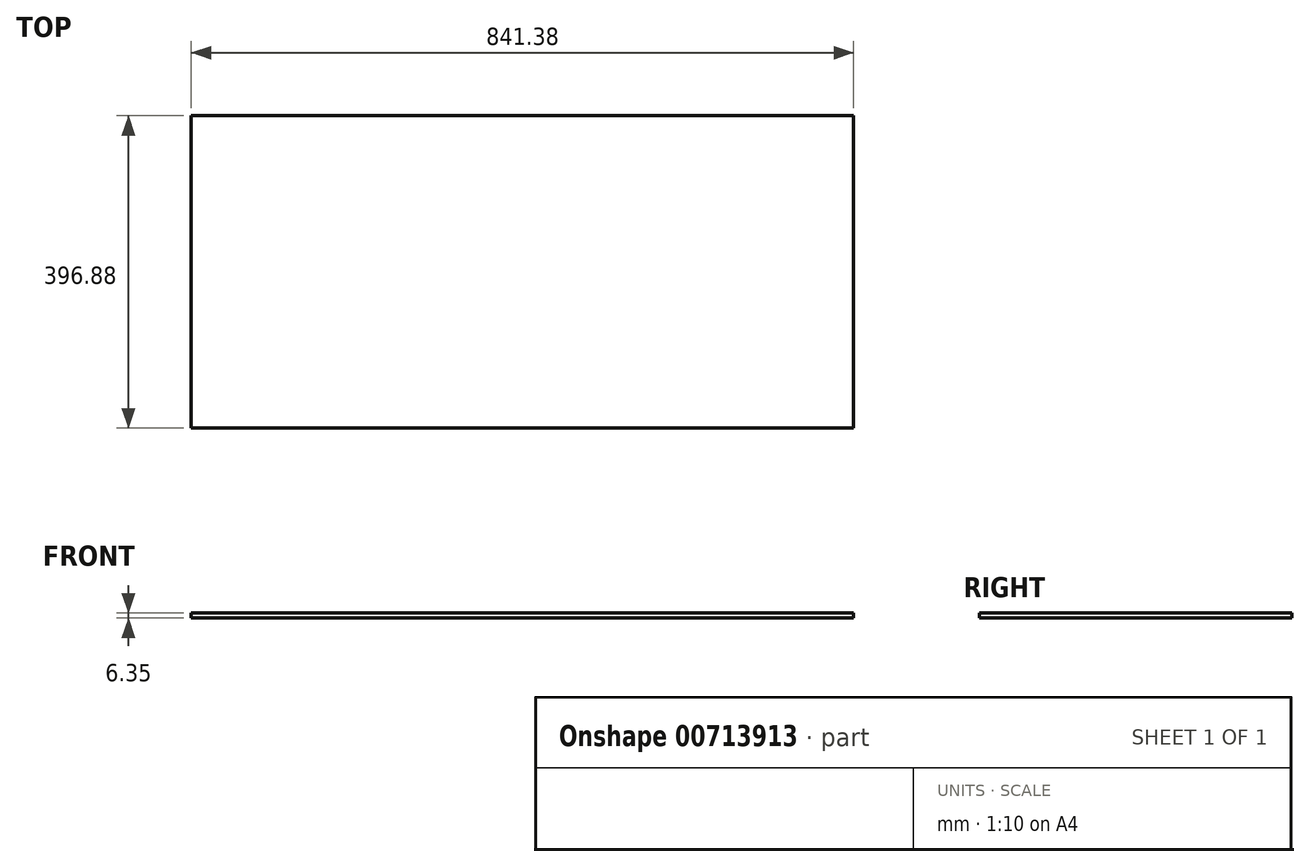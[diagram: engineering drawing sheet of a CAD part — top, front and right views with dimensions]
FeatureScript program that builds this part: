
annotation { "Feature Type Name" : "Feature", "Feature Type Description" : "" }
export const myFeature = defineFeature(function(context is Context, id is Id, definition is map)
    precondition{}
    {
        {
            var Q0;
            Q0=qCreatedBy(makeId("Top.planeOp"),FACE);
            var sketch = newSketch(context, id + "F0", { "sketchPlane" : qUnion([Q0])});
            skLineSegment(sketch, "E0.bottom", {"start": v(420.69, 198.44) * mm, "end": v(-420.69, 198.44) * mm});
            skLineSegment(sketch, "E0.top", {"start": v(420.69, -198.44) * mm, "end": v(-420.69, -198.44) * mm});
            skLineSegment(sketch, "E0.left", {"start": v(420.69, 198.44) * mm, "end": v(420.69, -198.44) * mm});
            skLineSegment(sketch, "E0.right", {"start": v(-420.69, 198.44) * mm, "end": v(-420.69, -198.44) * mm});
            skPoint(sketch, "E0.middle", {"position": v(0, 0) * mm});
            skSolve(sketch);
        }
        {
            var Q0;
            Q0=makeQuery(id+"F0.imprint","IMPRINT",FACE,{"disambiguationData":[TD([[makeQuery(id+"F0.imprint","IMPRINT",EDGE,{"derivedFrom":sQuery(id+"F0.wireOp",EDGE,"E0.bottom")}),1.0]])]});
            extrude(context, id + "F1", {"entities" : qUnion([Q0]), "depth" : 6.35 * mm, "offsetDistance" : 25.4 * mm});
        }
    });
